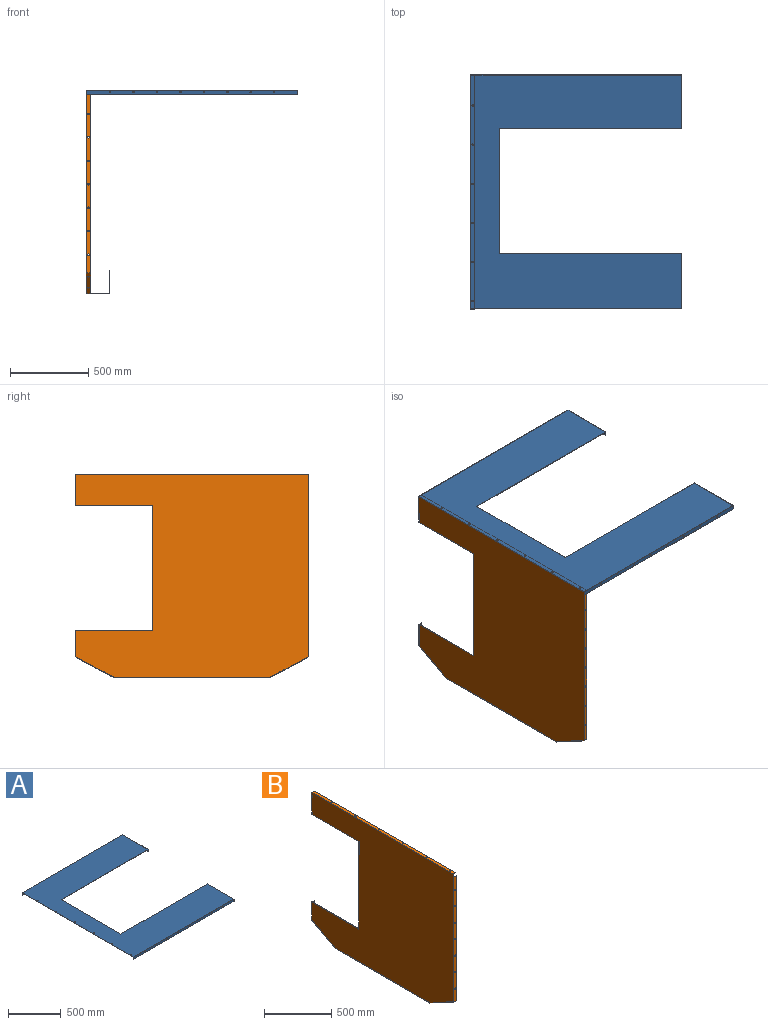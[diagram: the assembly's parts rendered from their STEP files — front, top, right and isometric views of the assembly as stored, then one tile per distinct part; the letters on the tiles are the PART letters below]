
ASSEMBLY  parts=2 mates=1
PART A: 56 faces, bbox 1352x1497x27 mm
  f0: cylinder r=5mm len=5mm, axis (1,0,0), area 15.7mm2, adj f1,f2,f3,f45
  f1: cylinder r=5mm len=5mm, axis (1,0,0), area 15.7mm2, adj f0,f2,f10,f45
  f2: plane 351.5x25mm, normal (-1,0,0), area 8630.5mm2, adj f0,f1,f3,f4,f5,f6,f7,f8
  f3: cylinder r=5mm len=5mm, axis (1,0,0), area 15.7mm2, adj f0,f2,f10,f45
  f4: plane 1168x27mm, normal (0,1,0), area 2386mm2, adj f2,f5,f21,f45,f48,f49
  f5: plane 1348x353.5mm, normal (0,0,-1), area 3399mm2, adj f2,f4,f11,f12,f43,f45
  f6: cylinder r=5mm len=5mm, axis (1,0,0), area 15.7mm2, adj f2,f7,f9,f45
  f7: cylinder r=5mm len=5mm, axis (1,0,0), area 15.7mm2, adj f2,f6,f8,f45
  f8: cylinder r=5mm len=5mm, axis (1,0,0), area 15.7mm2, adj f2,f7,f9,f45
  f9: cylinder r=5mm len=5mm, axis (1,0,0), area 15.7mm2, adj f2,f6,f8,f45
  f10: cylinder r=5mm len=5mm, axis (1,0,0), area 15.7mm2, adj f1,f2,f3,f45
  f11: plane 1346x25mm, normal (0,1,0), area 33021.7mm2, adj f2,f5,f12,f13,f14,f15,f16,f17
  f12: plane 25x2mm, normal (-1,0,0), area 50mm2, adj f5,f11,f43,f49
  f13: cylinder r=5mm len=10mm, axis (0,1,0), area 62.8mm2, adj f11,f43
  f14: cylinder r=5mm len=10mm, axis (0,1,0), area 62.8mm2, adj f11,f43
  f15: cylinder r=5mm len=10mm, axis (0,1,0), area 62.8mm2, adj f11,f43
  f16: cylinder r=5mm len=10mm, axis (0,1,0), area 62.8mm2, adj f11,f43
  f17: cylinder r=5mm len=10mm, axis (0,1,0), area 62.8mm2, adj f11,f43
  f18: cylinder r=5mm len=10mm, axis (0,1,0), area 62.8mm2, adj f11,f43
  f19: cylinder r=5mm len=10mm, axis (0,1,0), area 62.8mm2, adj f11,f43
  f20: cylinder r=5mm len=10mm, axis (0,1,0), area 62.8mm2, adj f11,f43
  f21: plane 800x2mm, normal (1,0,0), area 1600mm2, adj f4,f22,f48,f49
  f22: plane 1168x27mm, normal (0,-1,0), area 2386mm2, adj f21,f23,f25,f46,f48,f49
  f23: plane 341.5x25mm, normal (-1,0,0), area 8380.4mm2, adj f22,f24,f25,f26,f27,f28,f29,f30
  f24: plane 1346x25mm, normal (0,-1,0), area 33021.7mm2, adj f23,f25,f34,f35,f36,f37,f38,f39
  f25: plane 1348x343.5mm, normal (0,0,-1), area 3379mm2, adj f22,f23,f24,f42,f46,f47
  f26: cylinder r=5mm len=5mm, axis (1,0,0), area 15.7mm2, adj f23,f27,f29,f46
  f27: cylinder r=5mm len=5mm, axis (1,0,0), area 15.7mm2, adj f23,f26,f28,f46
  f28: cylinder r=5mm len=5mm, axis (1,0,0), area 15.7mm2, adj f23,f27,f29,f46
  f29: cylinder r=5mm len=5mm, axis (1,0,0), area 15.7mm2, adj f23,f26,f28,f46
  f30: cylinder r=5mm len=5mm, axis (1,0,0), area 15.7mm2, adj f23,f31,f33,f46
  f31: cylinder r=5mm len=5mm, axis (1,0,0), area 15.7mm2, adj f23,f30,f32,f46
  f32: cylinder r=5mm len=5mm, axis (1,0,0), area 15.7mm2, adj f23,f31,f33,f46
  f33: cylinder r=5mm len=5mm, axis (1,0,0), area 15.7mm2, adj f23,f30,f32,f46
  f34: cylinder r=5mm len=10mm, axis (0,1,0), area 62.8mm2, adj f24,f42
  f35: cylinder r=5mm len=10mm, axis (0,1,0), area 62.8mm2, adj f24,f42
  f36: cylinder r=5mm len=10mm, axis (0,1,0), area 62.8mm2, adj f24,f42
  f37: cylinder r=5mm len=10mm, axis (0,1,0), area 62.8mm2, adj f24,f42
  f38: cylinder r=5mm len=10mm, axis (0,1,0), area 62.8mm2, adj f24,f42
  f39: cylinder r=5mm len=10mm, axis (0,1,0), area 62.8mm2, adj f24,f42
  f40: cylinder r=5mm len=10mm, axis (0,1,0), area 62.8mm2, adj f24,f42
  f41: cylinder r=5mm len=10mm, axis (0,1,0), area 62.8mm2, adj f24,f42
  f42: plane 1352x27mm, normal (0,1,0), area 35775.7mm2, adj f25,f34,f35,f36,f37,f38,f39,f40
  f43: plane 1352x27mm, normal (0,-1,0), area 35775.7mm2, adj f5,f12,f13,f14,f15,f16,f17,f18
  f44: plane 1497x2mm, normal (-1,0,0), area 2994mm2, adj f42,f43,f48,f49
  f45: plane 353.5x27mm, normal (1,0,0), area 9387.5mm2, adj f0,f1,f3,f4,f5,f6,f7,f8
  f46: plane 343.5x27mm, normal (1,0,0), area 9117.4mm2, adj f22,f25,f26,f27,f28,f29,f30,f31
  f47: plane 25x2mm, normal (-1,0,0), area 50mm2, adj f24,f25,f42,f49
  f48: plane 1497x1352mm, normal (0,0,1), area 1089072.6mm2, adj f4,f21,f22,f42,f43,f44,f45,f46
  f49: plane 1497x1350mm, normal (0,0,-1), area 1082294.6mm2, adj f2,f4,f11,f12,f21,f22,f23,f24
  f50: cylinder r=5mm len=10mm, axis (0,0,1), area 62.8mm2, adj f48,f49
  f51: cylinder r=5mm len=10mm, axis (0,0,1), area 62.8mm2, adj f48,f49
  f52: cylinder r=5mm len=10mm, axis (0,0,1), area 62.8mm2, adj f48,f49
  f53: cylinder r=5mm len=10mm, axis (0,0,1), area 62.8mm2, adj f48,f49
  f54: cylinder r=5mm len=10mm, axis (0,0,1), area 62.8mm2, adj f48,f49
  f55: cylinder r=5mm len=10mm, axis (0,0,1), area 62.8mm2, adj f48,f49
PART B: 59 faces, bbox 151x1497x1300.5 mm
  f0: plane 173x2mm, normal (1,0,0), area 346mm2, adj f1,f2,f47,f50
  f1: plane 173x25mm, normal (0,-1,0), area 4246.5mm2, adj f0,f2,f3,f49,f50
  f2: plane 498x27mm, normal (0,0,-1), area 1046mm2, adj f0,f1,f4,f34,f47,f49
  f3: cylinder r=5mm len=10mm, axis (0,1,0), area 62.8mm2, adj f1,f47
  f4: plane 800x2mm, normal (0,1,0), area 1600mm2, adj f2,f5,f34,f49
  f5: plane 498x27mm, normal (0,0,1), area 1046mm2, adj f4,f6,f16,f19,f34,f49
  f6: plane 165.53x25mm, normal (0,-1,0), area 4059.8mm2, adj f5,f19,f20,f36,f49
  f7: plane 25x5mm, normal (0,0,1), area 125mm2, adj f8,f19,f36,f49
  f8: plane 25x2mm, normal (0,-1,0), area 50mm2, adj f7,f9,f19,f49
  f9: plane 996.42x151mm, normal (0,0,-1), area 112873.3mm2, adj f8,f10,f12,f13,f17,f18,f19,f21
  f10: plane 149x148mm, normal (0,1,0), area 590mm2, adj f9,f11,f24,f25,f26,f49
  f11: plane 742.17x147mm, normal (0,0,1), area 109099.1mm2, adj f10,f12,f25,f49
  f12: plane 149x148mm, normal (0,-1,0), area 590mm2, adj f9,f11,f24,f25,f26,f49
  f13: plane 25x2mm, normal (0,1,0), area 50mm2, adj f9,f14,f21,f49
  f14: plane 25x5.88mm, normal (0,0,1), area 147.1mm2, adj f13,f21,f40,f49
  f15: plane 1138.53x25mm, normal (0,1,0), area 27913.6mm2, adj f21,f27,f28,f29,f30,f31,f32,f33
  f16: plane 167x27mm, normal (0,1,0), area 4423.8mm2, adj f5,f17,f19,f20,f23,f34,f35
  f17: plane 250.29x133.5mm, normal (0,0.47,-0.88), area 567.3mm2, adj f9,f16,f23,f34
  f18: plane 250.29x133.5mm, normal (0,-0.47,-0.88), area 567.3mm2, adj f9,f22,f34,f43
  f19: plane 300.5x256.29mm, normal (1,0,0), area 909.5mm2, adj f5,f6,f7,f8,f9,f16,f35,f36
  f20: cylinder r=5mm len=10mm, axis (0,1,0), area 62.8mm2, adj f6,f16
  f21: plane 1273.5x257.17mm, normal (1,0,0), area 2857.3mm2, adj f9,f13,f14,f15,f39,f40,f43,f45
  f22: plane 250.79x133.77mm, normal (1,0,0), area 66.8mm2, adj f9,f18,f39,f43
  f23: plane 250.79x133.77mm, normal (1,0,0), area 66.8mm2, adj f9,f16,f17,f35
  f24: plane 742.17x148mm, normal (1,0,0), area 109841.3mm2, adj f9,f10,f12,f26
  f25: plane 742.17x146mm, normal (-1,0,0), area 108356.9mm2, adj f10,f11,f12,f26
  f26: plane 742.17x2mm, normal (0,0,1), area 1484.3mm2, adj f10,f12,f24,f25
  f27: cylinder r=5mm len=10mm, axis (0,1,0), area 62.8mm2, adj f15,f43
  f28: cylinder r=5mm len=10mm, axis (0,1,0), area 62.8mm2, adj f15,f43
  f29: cylinder r=5mm len=10mm, axis (0,1,0), area 62.8mm2, adj f15,f43
  f30: cylinder r=5mm len=10mm, axis (0,1,0), area 62.8mm2, adj f15,f43
  f31: cylinder r=5mm len=10mm, axis (0,1,0), area 62.8mm2, adj f15,f43
  f32: cylinder r=5mm len=10mm, axis (0,1,0), area 62.8mm2, adj f15,f43
  f33: cylinder r=5mm len=10mm, axis (0,1,0), area 62.8mm2, adj f15,f43
  f34: plane 1497x1300.5mm, normal (-1,0,0), area 1515034.8mm2, adj f2,f4,f5,f9,f16,f17,f18,f43
  f35: plane 250.79x133.77mm, normal (0,0.47,-0.88), area 6948.8mm2, adj f9,f16,f19,f23,f37,f38
  f36: plane 249.29x132.97mm, normal (0,-0.47,0.88), area 6906.3mm2, adj f6,f7,f19,f37,f38,f49
  f37: cylinder r=5mm len=10mm, axis (0,-0.47,0.88), area 62.8mm2, adj f35,f36
  f38: cylinder r=5mm len=10mm, axis (0,-0.47,0.88), area 62.8mm2, adj f35,f36
  f39: plane 250.79x133.77mm, normal (0,-0.47,-0.88), area 6948.8mm2, adj f9,f21,f22,f41,f42,f43
  f40: plane 249.29x132.97mm, normal (0,0.47,0.88), area 6906.3mm2, adj f14,f15,f21,f41,f42,f49
  f41: cylinder r=5mm len=10mm, axis (0,0.47,0.88), area 62.8mm2, adj f39,f40
  f42: cylinder r=5mm len=10mm, axis (0,0.47,0.88), area 62.8mm2, adj f39,f40
  f43: plane 1167x27mm, normal (0,-1,0), area 30277.6mm2, adj f18,f21,f22,f27,f28,f29,f30,f31
  f44: plane 23x2mm, normal (0,-1,0), area 46mm2, adj f46,f49,f51,f52
  f45: plane 25x2mm, normal (0,0,1), area 50mm2, adj f15,f21,f43,f49
  f46: plane 1491x2mm, normal (1,0,0), area 2982mm2, adj f44,f48,f51,f52
  f47: plane 200x27mm, normal (0,1,0), area 4646.5mm2, adj f0,f2,f3,f34,f49,f50,f51
  f48: plane 23x2mm, normal (0,1,0), area 46mm2, adj f46,f49,f51,f52
  f49: plane 1497x1300.5mm, normal (1,0,0), area 1506322mm2, adj f1,f2,f4,f5,f6,f7,f8,f9
  f50: plane 25x2mm, normal (0,0,1), area 50mm2, adj f0,f1,f47,f49
  f51: plane 1497x25mm, normal (0,0,1), area 36815.8mm2, adj f34,f43,f44,f46,f47,f48,f49,f53
  f52: plane 1491x23mm, normal (0,0,-1), area 33821.8mm2, adj f44,f46,f48,f49,f53,f54,f55,f56
  f53: cylinder r=5mm len=10mm, axis (0,0,-1), area 62.8mm2, adj f51,f52
  f54: cylinder r=5mm len=10mm, axis (0,0,-1), area 62.8mm2, adj f51,f52
  f55: cylinder r=5mm len=10mm, axis (0,0,-1), area 62.8mm2, adj f51,f52
  f56: cylinder r=5mm len=10mm, axis (0,0,-1), area 62.8mm2, adj f51,f52
  f57: cylinder r=5mm len=10mm, axis (0,0,-1), area 62.8mm2, adj f51,f52
  f58: cylinder r=5mm len=10mm, axis (0,0,-1), area 62.8mm2, adj f51,f52
PLACE A at identity fixed
PLACE B at identity
MATE fastened B.f58 <-> A.f55  axis (0,0,1) through (-1339,52,0)mm
